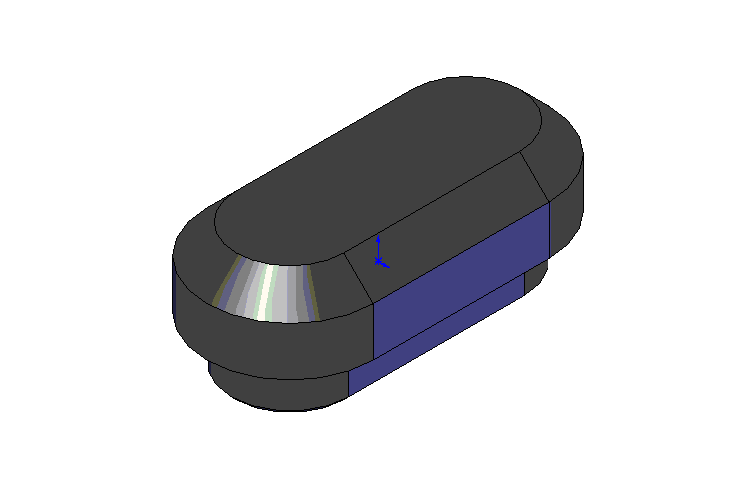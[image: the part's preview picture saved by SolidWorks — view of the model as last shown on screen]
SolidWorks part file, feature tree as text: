
SOLIDWORKS PART (.sldprt)
format: sldprt  version: not decoded by parser v0  size: 198,656 bytes
history: native  units: mm
features: plane x3, sketch x2, extrude x2, chamfer x2, material x1, shell x1 (+10 scaffold rows collapsed)
feature tree (21):
  scaffold x10  (default folders/planes/origin — collapsed)
  material  "Matériau <non spécifié>"
  plane  "Plan de face"
  plane  "Plan de dessus"
  plane  "Plan de droite"
  sketch  "Esquisse1"  dims[D1=35.0mm D2=17.0mm]
  extrude  "Extrusion1"  Depth=8mm
  chamfer  "Chanfrein1"  Distance=3mm Angle=45deg
  shell  "Coque1"  Thickness=4mm
  sketch  "Esquisse2"  dims[D1=1.5mm]
  extrude  "Extrusion2"  Depth=5mm
  chamfer  "Chanfrein2"  Distance=0.5mm Angle=45deg
decode coverage: 7 of 7 modeling features carry decoded parameters
note: suppression state not decoded; provenance and decode notes live in map.json
